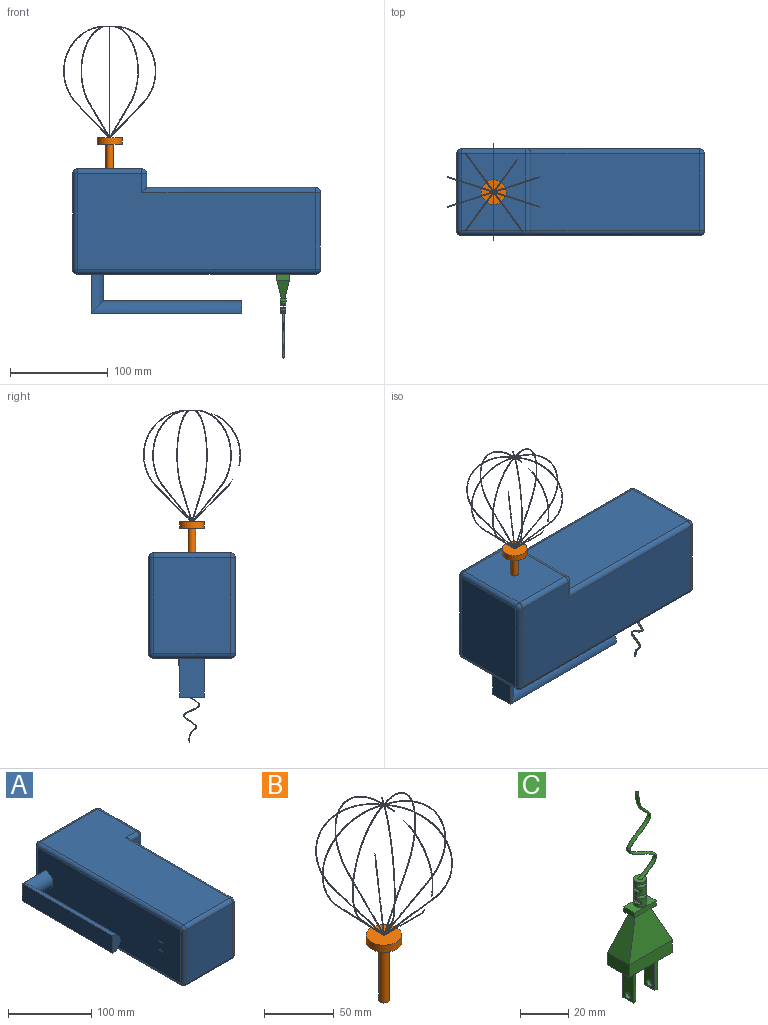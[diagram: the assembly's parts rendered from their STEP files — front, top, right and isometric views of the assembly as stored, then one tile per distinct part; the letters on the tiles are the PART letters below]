
ASSEMBLY  parts=3 mates=2
PART A: 52 faces, bbox 147.8x254x88.9 mm
  f0: plane 243.84x78.74mm, normal (-1,0,0), area 18926.4mm2, adj f11,f12,f27,f36,f37,f41,f42,f43
  f1: plane 97.79x78.74mm, normal (0,1,0), area 7700mm2, adj f30,f35,f38,f41
  f2: plane 78.74x78.74mm, normal (0,-1,0), area 6200mm2, adj f17,f26,f27,f28
  f3: plane 172.72x78.74mm, normal (1,0,0), area 13600mm2, adj f4,f16,f17,f18
  f4: plane 78.74x13.97mm, normal (0,-1,0), area 1100mm2, adj f3,f15,f19,f20
  f5: plane 78.74x66.04mm, normal (1,0,0), area 5154.4mm2, adj f13,f20,f25,f29,f30
  f6: plane 243.84x97.79mm, normal (0,0,1), area 20458mm2, adj f15,f16,f25,f26,f35,f36
  f7: plane 243.84x97.79mm, normal (0,0,-1), area 20458mm2, adj f18,f19,f28,f29,f37,f38
  f8: plane 25.4x12.7mm, normal (0,-1,0), area 253.4mm2, adj f9,f10
  f9: plane 154.18x25.4mm, normal (-1,0,0), area 3916.3mm2, adj f8,f10,f12
  f10: cylinder r=12.7mm len=154.18mm, axis (0,-1,0), area 5829.1mm2, adj f8,f9,f11
  f11: cylinder r=12.7mm len=39.88mm, axis (-1,0,0), area 1268.7mm2, adj f0,f10,f12
  f12: plane 39.88x25.4mm, normal (0,1,0), area 1013.1mm2, adj f0,f9,f11
  f13: cylinder r=3.81mm len=38.1mm, axis (1,0,0), area 912.1mm2, adj f5,f14
  f14: plane 7.62x7.62mm, normal (1,0,0), area 45.6mm2, adj f13
  f15: cylinder r=5.08mm len=19.05mm, axis (-1,0,0), area 126.2mm2, adj f4,f6,f16,f21
  f16: cylinder r=5.08mm len=177.8mm, axis (0,-1,0), area 1393mm2, adj f3,f6,f15,f22
  f17: cylinder r=5.08mm len=78.74mm, axis (0,0,-1), area 628.3mm2, adj f2,f3,f22,f23
  f18: cylinder r=5.08mm len=177.8mm, axis (0,1,0), area 1393mm2, adj f3,f7,f19,f23
  f19: cylinder r=5.08mm len=19.05mm, axis (1,0,0), area 126.2mm2, adj f4,f7,f18,f24
  f20: cylinder r=5.08mm len=78.74mm, axis (0,0,-1), area 628.3mm2, adj f4,f5,f21,f24
  f21: sphere r=5.08mm, area 40.5mm2, adj f15,f20,f25
  f22: sphere r=5.08mm, area 40.5mm2, adj f16,f17,f26
  f23: sphere r=5.08mm, area 40.5mm2, adj f17,f18,f28
  f24: sphere r=5.08mm, area 40.5mm2, adj f19,f20,f29
  f25: cylinder r=5.08mm len=66.04mm, axis (0,-1,0), area 527mm2, adj f5,f6,f21,f31
  f26: cylinder r=5.08mm len=78.74mm, axis (-1,0,0), area 628.3mm2, adj f2,f6,f22,f32
  f27: cylinder r=5.08mm len=78.74mm, axis (0,0,-1), area 628.3mm2, adj f0,f2,f32,f33
  f28: cylinder r=5.08mm len=78.74mm, axis (1,0,0), area 628.3mm2, adj f2,f7,f23,f33
  f29: cylinder r=5.08mm len=66.04mm, axis (0,1,0), area 527mm2, adj f5,f7,f24,f34
  f30: cylinder r=5.08mm len=78.74mm, axis (0,0,-1), area 628.3mm2, adj f1,f5,f31,f34
  f31: sphere r=5.08mm, area 40.5mm2, adj f25,f30,f35
  f32: sphere r=5.08mm, area 40.5mm2, adj f26,f27,f36
  f33: sphere r=5.08mm, area 40.5mm2, adj f27,f28,f37
  f34: sphere r=5.08mm, area 40.5mm2, adj f29,f30,f38
  f35: cylinder r=5.08mm len=97.79mm, axis (1,0,0), area 780.3mm2, adj f1,f6,f31,f39
  f36: cylinder r=5.08mm len=243.84mm, axis (0,1,0), area 1945.8mm2, adj f0,f6,f32,f39
  f37: cylinder r=5.08mm len=243.84mm, axis (0,-1,0), area 1945.8mm2, adj f0,f7,f33,f40
  f38: cylinder r=5.08mm len=97.79mm, axis (-1,0,0), area 780.3mm2, adj f1,f7,f34,f40
  f39: sphere r=5.08mm, area 40.5mm2, adj f35,f36,f41
  f40: sphere r=5.08mm, area 40.5mm2, adj f37,f38,f41
  f41: cylinder r=5.08mm len=78.74mm, axis (0,0,-1), area 628.3mm2, adj f0,f1,f39,f40
  f42: plane 17.78x1.59mm, normal (0,1,0), area 28.2mm2, adj f0,f43,f45,f46
  f43: plane 17.78x6.35mm, normal (0,0,-1), area 112.9mm2, adj f0,f42,f44,f46
  f44: plane 17.78x1.59mm, normal (0,-1,0), area 28.2mm2, adj f0,f43,f45,f46
  f45: plane 17.78x6.35mm, normal (0,0,1), area 112.9mm2, adj f0,f42,f44,f46
  f46: plane 6.35x1.59mm, normal (-1,0,0), area 10.1mm2, adj f42,f43,f44,f45
  f47: plane 17.78x1.59mm, normal (0,1,0), area 28.2mm2, adj f0,f48,f50,f51
  f48: plane 17.78x6.35mm, normal (0,0,-1), area 112.9mm2, adj f0,f47,f49,f51
  f49: plane 17.78x1.59mm, normal (0,-1,0), area 28.2mm2, adj f0,f48,f50,f51
  f50: plane 17.78x6.35mm, normal (0,0,1), area 112.9mm2, adj f0,f47,f49,f51
  f51: plane 6.35x1.59mm, normal (-1,0,0), area 10.1mm2, adj f47,f48,f49,f50
PART B: 25 faces, bbox 94.5x98.8x171.9 mm
  f0: bspline ~78.9x40.34mm, area 177.6mm2, adj f2,f8,f24
  f1: bspline ~36.1x29.37mm, area 79.9mm2, adj f3,f10,f15,f23
  f2: bspline ~78.87x47.29mm, area 177.6mm2, adj f0,f5,f21
  f3: bspline ~36.13x34.44mm, area 79.9mm2, adj f1,f4,f10,f22
  f4: bspline ~36.13x34.44mm, area 79.9mm2, adj f3,f10,f18,f19
  f5: bspline ~78.97x47.3mm, area 177.5mm2, adj f2,f6,f20
  f6: bspline ~78.9x40.34mm, area 177.6mm2, adj f5,f7,f16
  f7: bspline ~78.82x49.12mm, area 177.7mm2, adj f6,f15,f23
  f8: bspline ~78.9x49.69mm, area 177.3mm2, adj f0,f14,f17
  f9: cylinder r=12.7mm len=25.4mm, axis (0,0,-1), area 506.7mm2, adj f10,f11
  f10: plane 25.45x25.45mm, normal (0,0,1), area 506.3mm2, adj f1,f3,f4,f9,f14,f15,f16,f18
  f11: plane 25.4x25.4mm, normal (0,0,-1), area 461.1mm2, adj f9,f12
  f12: cylinder r=3.81mm len=50.8mm, axis (0,0,1), area 1216.1mm2, adj f11,f13
  f13: plane 7.62x7.62mm, normal (0,0,-1), area 45.6mm2, adj f12
  f14: bspline ~36.59x36.54mm, area 79.9mm2, adj f8,f10,f18,f24
  f15: bspline ~36.56x36.51mm, area 79.9mm2, adj f1,f7,f10,f16
  f16: bspline ~36.14x29.33mm, area 79.9mm2, adj f6,f10,f15,f20
  f17: bspline ~78.91x40.36mm, area 177.3mm2, adj f8,f18,f19
  f18: bspline ~36.1x29.37mm, area 79.9mm2, adj f4,f10,f14,f17
  f19: bspline ~78.9x47.31mm, area 177.3mm2, adj f4,f17,f22
  f20: bspline ~36.14x34.36mm, area 79.9mm2, adj f5,f10,f16,f21
  f21: bspline ~36.14x34.36mm, area 79.9mm2, adj f2,f10,f20,f24
  f22: bspline ~78.9x47.32mm, area 177.2mm2, adj f3,f19,f23
  f23: bspline ~78.9x40.37mm, area 177.2mm2, adj f1,f7,f22
  f24: bspline ~36.14x29.33mm, area 79.9mm2, adj f0,f10,f14,f21
PART C: 63 faces, bbox 25.4x12.7x103.7 mm
  f0: cylinder r=2.78mm len=12.7mm, axis (0,0,-1), area 139.2mm2, adj f15,f16,f17,f18,f19,f20,f21,f22
  f1: plane 25.4x6.35mm, normal (0,1,0), area 161.3mm2, adj f2,f4,f5,f9
  f2: plane 12.7x6.35mm, normal (-1,0,0), area 80.6mm2, adj f1,f3,f5,f6
  f3: plane 25.4x6.35mm, normal (0,-1,0), area 161.3mm2, adj f2,f4,f5,f7
  f4: plane 12.7x6.35mm, normal (1,0,0), area 80.6mm2, adj f1,f3,f5,f8
  f5: plane 25.4x12.7mm, normal (0,0,-1), area 302.4mm2, adj f1,f2,f3,f4,f43,f44,f45,f46
  f6: plane 19.05x12.7mm, normal (-0.92,0,0.4), area 167.6mm2, adj f2,f7,f9,f10
  f7: plane 25.4x19.05mm, normal (0,-0.97,0.24), area 330.9mm2, adj f3,f6,f8,f10
  f8: plane 19.05x12.7mm, normal (0.91,0,0.41), area 168.6mm2, adj f4,f7,f9,f10
  f9: plane 25.4x19.05mm, normal (0,0.97,0.23), area 330.5mm2, adj f1,f6,f8,f10
  f10: plane 12.7x6.35mm, normal (0,0,-1), area 52.3mm2, adj f6,f7,f8,f9,f11,f12,f13,f14
  f11: plane 6.35x2.54mm, normal (1,0,0), area 16.1mm2, adj f10,f12,f14,f15
  f12: plane 12.7x2.54mm, normal (0,1,0), area 32.3mm2, adj f10,f11,f13,f15
  f13: plane 6.35x2.54mm, normal (-1,0,0), area 16.1mm2, adj f10,f12,f14,f15
  f14: plane 12.7x2.54mm, normal (0,-1,0), area 32.3mm2, adj f10,f11,f13,f15
  f15: plane 12.7x6.35mm, normal (0,0,1), area 56.4mm2, adj f0,f11,f12,f13,f14
  f16: plane 5.56x5.56mm, normal (0,0,1), area 21.8mm2, adj f0,f42
  f17: plane 4.87x1.43mm, normal (0,0,1), area 5mm2, adj f0,f19
  f18: plane 4.87x1.43mm, normal (0,0,-1), area 5mm2, adj f0,f19
  f19: plane 4.87x1.52mm, normal (-1,0,0), area 7.4mm2, adj f0,f17,f18
  f20: plane 4.87x1.43mm, normal (0,0,1), area 5mm2, adj f0,f22
  f21: plane 4.87x1.43mm, normal (0,0,-1), area 5mm2, adj f0,f22
  f22: plane 4.87x1.52mm, normal (-1,0,0), area 7.4mm2, adj f0,f20,f21
  f23: plane 5.02x1.59mm, normal (0,0,1), area 5.7mm2, adj f0,f25
  f24: plane 5.02x1.59mm, normal (0,0,-1), area 5.7mm2, adj f0,f25
  f25: plane 5.02x1.52mm, normal (1,0,0), area 7.6mm2, adj f0,f23,f24
  f26: plane 5.02x1.59mm, normal (0,0,1), area 5.7mm2, adj f0,f28
  f27: plane 5.02x1.59mm, normal (0,0,-1), area 5.7mm2, adj f0,f28
  f28: plane 5.02x1.52mm, normal (1,0,0), area 7.6mm2, adj f0,f26,f27
  f29: plane 5.4x2.12mm, normal (0,0,1), area 8.5mm2, adj f0,f31
  f30: plane 5.4x2.12mm, normal (0,0,-1), area 8.5mm2, adj f0,f31
  f31: plane 5.4x1.52mm, normal (0,-1,0), area 8.2mm2, adj f0,f29,f30
  f32: plane 5.4x2.12mm, normal (0,0,1), area 8.5mm2, adj f0,f34
  f33: plane 5.4x2.12mm, normal (0,0,-1), area 8.5mm2, adj f0,f34
  f34: plane 5.4x1.52mm, normal (0,-1,0), area 8.2mm2, adj f0,f32,f33
  f35: plane 5.42x2.17mm, normal (0,0,1), area 8.8mm2, adj f0,f37
  f36: plane 5.42x2.17mm, normal (0,0,-1), area 8.8mm2, adj f0,f37
  f37: plane 5.42x1.52mm, normal (0,1,0), area 8.3mm2, adj f0,f35,f36
  f38: plane 5.42x2.17mm, normal (0,0,1), area 8.8mm2, adj f0,f40
  f39: plane 5.42x2.17mm, normal (0,0,-1), area 8.8mm2, adj f0,f40
  f40: plane 5.42x1.52mm, normal (0,1,0), area 8.3mm2, adj f0,f38,f39
  f41: plane 1.78x1.6mm, normal (-0.9,0,0.43), area 2.5mm2, adj f42
  f42: bspline ~45.25x16.67mm, area 281.3mm2, adj f16,f41
  f43: plane 17.27x1.59mm, normal (0,-1,0), area 27.4mm2, adj f5,f44,f46,f60
  f44: plane 17.27x6.35mm, normal (-1,0,0), area 101.8mm2, adj f5,f43,f45,f54,f62
  f45: plane 17.27x1.59mm, normal (0,1,0), area 27.4mm2, adj f5,f44,f46,f61
  f46: plane 17.27x6.35mm, normal (1,0,0), area 101.8mm2, adj f5,f43,f45,f54,f59
  f47: plane 5.33x0.57mm, normal (0,0,-1), area 3mm2, adj f59,f60,f61,f62
  f48: plane 17.27x1.59mm, normal (0,-1,0), area 27.4mm2, adj f5,f49,f51,f55
  f49: plane 17.27x6.35mm, normal (-1,0,0), area 101.8mm2, adj f5,f48,f50,f53,f56
  f50: plane 17.27x1.59mm, normal (0,1,0), area 27.4mm2, adj f5,f49,f51,f58
  f51: plane 17.27x6.35mm, normal (1,0,0), area 101.8mm2, adj f5,f48,f50,f53,f57
  f52: plane 5.33x0.57mm, normal (0,0,-1), area 3mm2, adj f55,f56,f57,f58
  f53: cylinder r=1.59mm len=3.18mm, axis (-1,0,0), area 15.8mm2, adj f49,f51
  f54: cylinder r=1.59mm len=3.18mm, axis (-1,0,0), area 15.8mm2, adj f44,f46
  f55: cylinder r=0.51mm len=1.59mm, axis (1,0,0), area 1mm2, adj f48,f52,f56,f57
  f56: cylinder r=0.51mm len=6.35mm, axis (0,-1,0), area 4.8mm2, adj f49,f52,f55,f58
  f57: cylinder r=0.51mm len=6.35mm, axis (0,1,0), area 4.8mm2, adj f51,f52,f55,f58
  f58: cylinder r=0.51mm len=1.59mm, axis (-1,0,0), area 1mm2, adj f50,f52,f56,f57
  f59: cylinder r=0.51mm len=6.35mm, axis (0,1,0), area 4.8mm2, adj f46,f47,f60,f61
  f60: cylinder r=0.51mm len=1.59mm, axis (1,0,0), area 1mm2, adj f43,f47,f59,f62
  f61: cylinder r=0.51mm len=1.59mm, axis (-1,0,0), area 1mm2, adj f45,f47,f59,f62
  f62: cylinder r=0.51mm len=6.35mm, axis (0,-1,0), area 4.8mm2, adj f44,f47,f60,f61
PLACE A rot(axis=(0.58,-0.58,0.58),120deg) t=(-530.66,542.63,-549.22)mm
PLACE B rot(axis=(-0.26,-0.02,-0.97),0deg) t=(-492.56,498.18,-415.87)mm
PLACE C rot(axis=(0.71,-0.71,0),180deg) t=(-321.11,512.15,-549.22)mm
MATE slider B.f12 <-> A.f13  axis (0,0,1) through (-492.56,498.18,-441.27)mm
MATE slider C.f47 <-> A.f0  axis (0,0,1) through (-314.76,505.8,-531.44)mm
